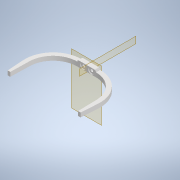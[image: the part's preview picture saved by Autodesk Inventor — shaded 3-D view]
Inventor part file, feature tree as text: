
AUTODESK INVENTOR PART (.ipt)
format: ipt  version: 2020 (Build 240168000, 168)  size: 174,080 bytes
history: native  units: mm
features: sketch x4, extrude x3, other x3, plane x2, hole x1, draft x1, mirror x1, reference x1
ambient origin geometry x8: Origin, YZ Plane, XZ Plane, XY Plane, X Axis, Y Axis, Z Axis, Center Point
bodies: Solid1 (feature_tree)
feature tree (16):
  plane  "Work Plane1"
  extrude  "Extrusion1"  Depth=1.5mm
  hole  "Hole1"  [1 undecoded]
  extrude  "Extrusion2"  Depth=50.0mm
  draft  "FaceDraft1"
  sketch  "Sketch5"  dims[d13=0.872665mm d15=50.0mm d16=3.0mm d17=5.0mm d18=0.0mm]
  plane  "Work Plane2"
  extrude  "Extrusion3"  Depth=5.0mm
  mirror  "Mirror1"
  sketch  "Sketch1"  dims[d0=5.0mm d1=0.0mm]
  reference  "Reference1"
  sketch  "Sketch2"  dims[d2=3.0mm d3=6.0mm d4=6.5mm d5=1.0mm d6=90.0deg d7=8.0mm d8=20.594885mm d9=1.5mm]
  sketch  "Sketch4"  dims[d10=2.0mm d11=0.0mm d12=0.0mm]
  parser-record x1  (decoder bookkeeping rows leaked as tree rows — omitted from the tree; the rows remain in map.json)
  other  "motorized2.iam"
  other  "servo_bracket:1"
note: 1 required parameter value undecoded (feature->parameter linkage not recoverable at this tier; creation-order binding heuristic only, values carry confidence <= 0.55)
note: 1 file-system path scrubbed to <path> (originals preserved in map.json)
